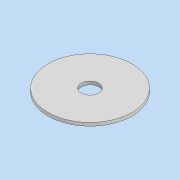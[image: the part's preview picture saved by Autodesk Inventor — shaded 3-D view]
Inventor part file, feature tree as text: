
AUTODESK INVENTOR PART (.ipt)
format: ipt  version: 2022 (Build 260153000, 153)  size: 80,896 bytes
history: native  units: in
note: dims shown in document units (in); Inventor stores cm internally (conversion verified against a paired STEP export)
features: extrude x1, sketch x1
ambient origin geometry x8: Origin, YZ Plane, XZ Plane, XY Plane, X Axis, Y Axis, Z Axis, Center Point
bodies: Solid1 (feature_tree)
feature tree (2):
  extrude  "Extrusion1"  Depth=0.0394in
  sketch  "Sketch1"  dims[d0=0.9984in d1=0.2067in d2=0.0394in d3=0.0in]
